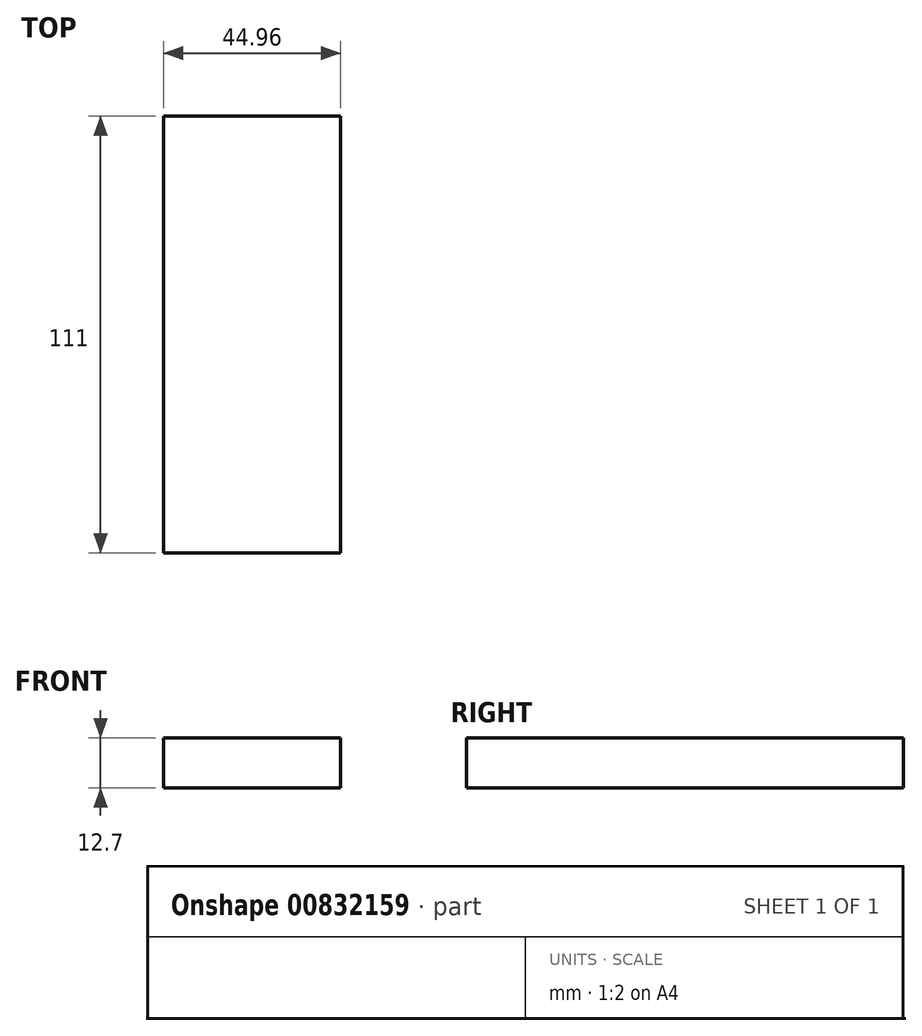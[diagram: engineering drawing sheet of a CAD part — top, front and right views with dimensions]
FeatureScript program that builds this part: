
annotation { "Feature Type Name" : "Feature", "Feature Type Description" : "" }
export const myFeature = defineFeature(function(context is Context, id is Id, definition is map)
    precondition{}
    {
        {
            var Q0;
            Q0=qCreatedBy(makeId("Top.planeOp"),FACE);
            var sketch = newSketch(context, id + "F0", { "sketchPlane" : qUnion([Q0])});
            skLineSegment(sketch, "E0.bottom", {"start": v(0, 0) * mm, "end": v(44.96, 0) * mm});
            skLineSegment(sketch, "E0.top", {"start": v(0, 111) * mm, "end": v(44.96, 111) * mm});
            skLineSegment(sketch, "E0.left", {"start": v(0, 0) * mm, "end": v(0, 111) * mm});
            skLineSegment(sketch, "E0.right", {"start": v(44.96, 0) * mm, "end": v(44.96, 111) * mm});
            skSolve(sketch);
        }
        {
            var Q0;
            Q0=qSketchRegion(id+"F0",true);
            extrude(context, id + "F1", {"entities" : qUnion([Q0]), "depth" : 12.7 * mm, "offsetDistance" : 25.4 * mm});
        }
    });
